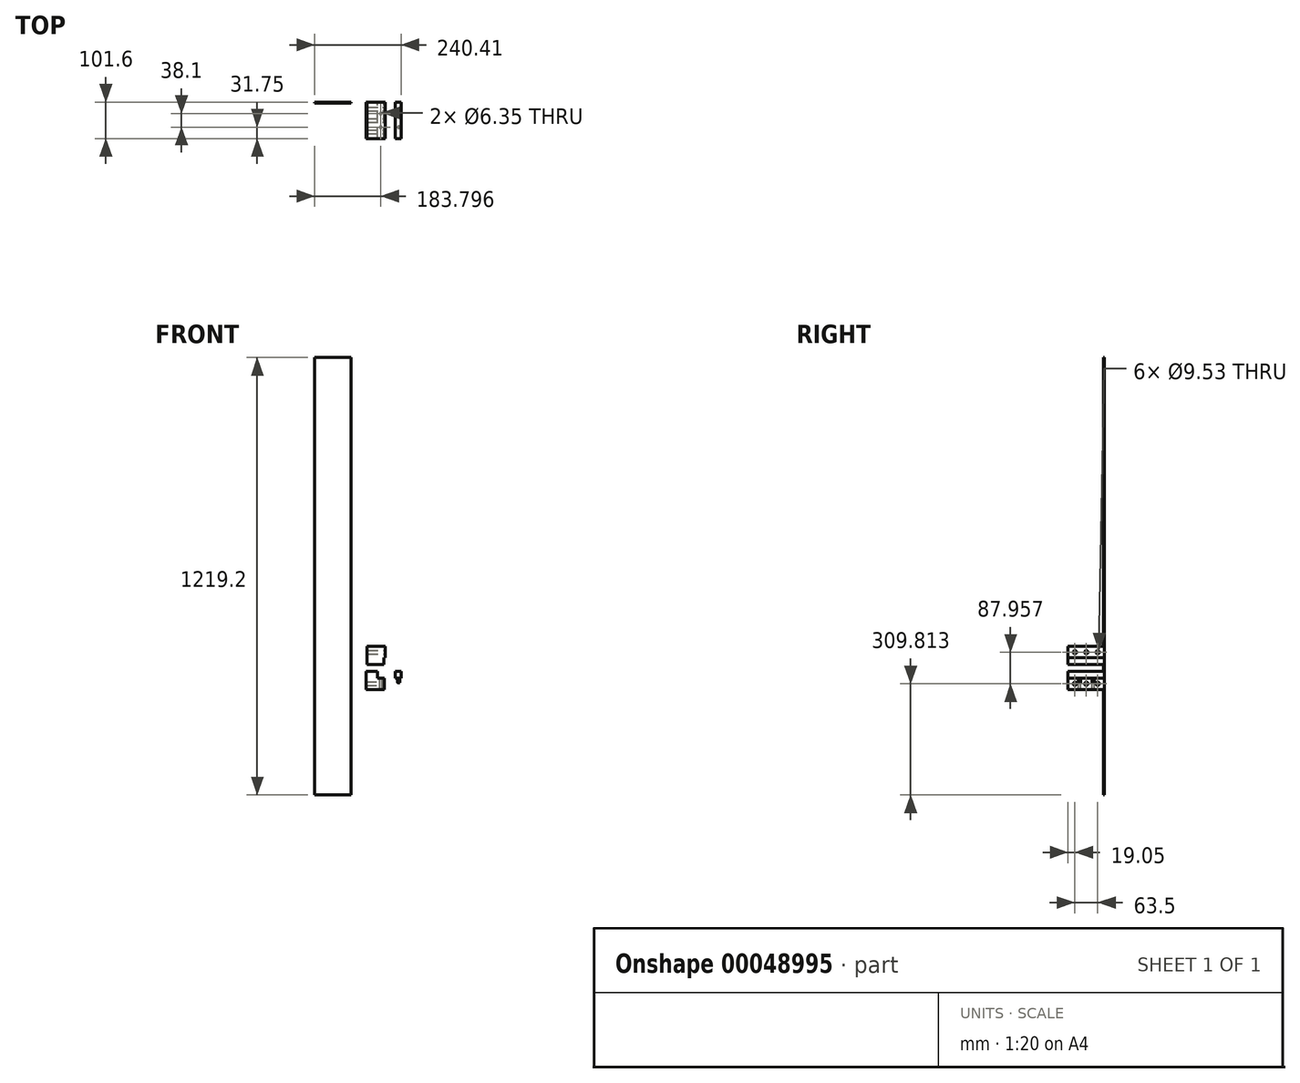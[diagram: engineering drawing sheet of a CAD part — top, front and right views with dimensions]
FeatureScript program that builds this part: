
annotation { "Feature Type Name" : "Feature", "Feature Type Description" : "" }
export const myFeature = defineFeature(function(context is Context, id is Id, definition is map)
    precondition{}
    {
        {
            var Q0;
            Q0=qCreatedBy(makeId("Front.planeOp"),FACE);
            var sketch = newSketch(context, id + "F0", { "sketchPlane" : qUnion([Q0])});
            skLineSegment(sketch, "E0", {"start": v(-72.63, 46.09) * mm, "end": v(-72.63, -4.71) * mm});
            skLineSegment(sketch, "E1", {"start": v(-72.63, -4.71) * mm, "end": v(-21.83, -4.71) * mm});
            skLineSegment(sketch, "E2", {"start": v(-21.83, -4.71) * mm, "end": v(-21.83, 27.04) * mm});
            skLineSegment(sketch, "E3", {"start": v(-21.83, 27.04) * mm, "end": v(-40.88, 27.04) * mm});
            skLineSegment(sketch, "E4", {"start": v(-40.88, 27.04) * mm, "end": v(-40.88, 46.09) * mm});
            skLineSegment(sketch, "E5", {"start": v(-40.88, 46.09) * mm, "end": v(-72.63, 46.09) * mm});
            skSolve(sketch);
        }
        {
            var Q0;
            Q0 = qSketchRegion(id + "F0", true);
            extrude(context, id + "F1", {"entities" : qUnion([Q0]), "depth" : 101.6 * mm});
        }
        {
            var Q0;
            Q0=makeQuery(id+"F1.opExtrude","SWEPT_FACE",FACE,{"disambiguationData":[OSD([sQuery(id+"F0.wireOp",EDGE,"E3")])]});
            var sketch = newSketch(context, id + "F2", { "sketchPlane" : qUnion([Q0])});
            skLineSegment(sketch, "E6.bottom", {"start": v(-21.83, -101.6) * mm, "end": v(-31.35, -101.6) * mm});
            skLineSegment(sketch, "E6.top", {"start": v(-21.83, -69.85) * mm, "end": v(-31.35, -69.85) * mm});
            skLineSegment(sketch, "E6.left", {"start": v(-21.83, -101.6) * mm, "end": v(-21.83, -69.85) * mm});
            skLineSegment(sketch, "E6.right", {"start": v(-31.35, -101.6) * mm, "end": v(-31.35, -69.85) * mm});
            skLineSegment(sketch, "E7.bottom", {"start": v(-21.83, 0) * mm, "end": v(-31.35, 0) * mm});
            skLineSegment(sketch, "E7.top", {"start": v(-21.83, -31.75) * mm, "end": v(-31.35, -31.75) * mm});
            skLineSegment(sketch, "E7.left", {"start": v(-21.83, 0) * mm, "end": v(-21.83, -31.75) * mm});
            skLineSegment(sketch, "E7.right", {"start": v(-31.35, 0) * mm, "end": v(-31.35, -31.75) * mm});
            skSolve(sketch);
        }
        {
            var Q0;
            Q0=sQuery(id+"F2.wireOp",VERTEX,"E6.top.end");
            var Q1;
            Q1=sQuery(id+"F2.wireOp",VERTEX,"E7.right.end");
            var Q2;
            Q2=makeQuery(id+"F1.opExtrude","SWEPT_BODY",BODY,{"disambiguationData":[OSD([sQuery(id+"F0.wireOp",EDGE,"E0"),sQuery(id+"F0.wireOp",EDGE,"E1"),sQuery(id+"F0.wireOp",EDGE,"E2"),sQuery(id+"F0.wireOp",EDGE,"E3"),sQuery(id+"F0.wireOp",EDGE,"E4"),sQuery(id+"F0.wireOp",EDGE,"E5")])]});
            hole(context, id + "F3", {"style" : HoleStyle.SIMPLE, "holeDiameter" : 6.35 * mm, "endStyle" : HoleEndStyle.THROUGH, "locations" : qUnion([Q0, Q1]), "scope" : qUnion([Q2])});
        }
        {
            var Q0;
            Q0=makeQuery(id+"F1.opExtrude","SWEPT_FACE",FACE,{"disambiguationData":[OSD([sQuery(id+"F0.wireOp",EDGE,"E2")])]});
            var sketch = newSketch(context, id + "F4", { "sketchPlane" : qUnion([Q0])});
            skLineSegment(sketch, "E8.bottom", {"start": v(-101.6, -4.71) * mm, "end": v(-82.55, -4.71) * mm});
            skLineSegment(sketch, "E8.top", {"start": v(-101.6, 11.16) * mm, "end": v(-82.55, 11.16) * mm});
            skLineSegment(sketch, "E8.left", {"start": v(-101.6, -4.71) * mm, "end": v(-101.6, 11.16) * mm});
            skLineSegment(sketch, "E8.right", {"start": v(-82.55, -4.71) * mm, "end": v(-82.55, 11.16) * mm});
            skLineSegment(sketch, "E9.bottom", {"start": v(0, -4.71) * mm, "end": v(-50.8, -4.71) * mm});
            skLineSegment(sketch, "E9.top", {"start": v(0, 11.16) * mm, "end": v(-50.8, 11.16) * mm});
            skLineSegment(sketch, "E9.left", {"start": v(0, -4.71) * mm, "end": v(0, 11.16) * mm});
            skLineSegment(sketch, "E9.right", {"start": v(-50.8, -4.71) * mm, "end": v(-50.8, 11.16) * mm});
            skLineSegment(sketch, "E10.bottom", {"start": v(0, -4.71) * mm, "end": v(-25.4, -4.71) * mm});
            skLineSegment(sketch, "E10.top", {"start": v(0, 11.16) * mm, "end": v(-25.4, 11.16) * mm});
            skLineSegment(sketch, "E10.right", {"start": v(-25.4, -4.71) * mm, "end": v(-25.4, 11.16) * mm});
            skLineSegment(sketch, "E11.bottom", {"start": v(0, -4.71) * mm, "end": v(-19.05, -4.71) * mm});
            skLineSegment(sketch, "E11.top", {"start": v(0, 11.16) * mm, "end": v(-19.05, 11.16) * mm});
            skLineSegment(sketch, "E11.right", {"start": v(-19.05, -4.71) * mm, "end": v(-19.05, 11.16) * mm});
            skSolve(sketch);
        }
        {
            var Q0;
            Q0=sQuery(id+"F4.wireOp",VERTEX,"E8.right.end");
            var Q1;
            Q1=sQuery(id+"F4.wireOp",VERTEX,"E9.right.end");
            var Q2;
            Q2=sQuery(id+"F4.wireOp",VERTEX,"E11.right.end");
            var Q3;
            Q3=makeQuery(id+"F1.opExtrude","SWEPT_BODY",BODY,{"disambiguationData":[OSD([sQuery(id+"F0.wireOp",EDGE,"E0"),sQuery(id+"F0.wireOp",EDGE,"E1"),sQuery(id+"F0.wireOp",EDGE,"E2"),sQuery(id+"F0.wireOp",EDGE,"E3"),sQuery(id+"F0.wireOp",EDGE,"E4"),sQuery(id+"F0.wireOp",EDGE,"E5")])]});
            hole(context, id + "F5", {"style" : HoleStyle.SIMPLE, "holeDiameter" : 9.52 * mm, "endStyle" : HoleEndStyle.THROUGH, "locations" : qUnion([Q0, Q1, Q2]), "scope" : qUnion([Q3])});
        }
        {
            var Q0;
            Q0=qCreatedBy(makeId("Front.planeOp"),FACE);
            var sketch = newSketch(context, id + "F6", { "sketchPlane" : qUnion([Q0])});
            skLineSegment(sketch, "E12.bottom", {"start": v(9.39, 45.44) * mm, "end": v(25.26, 45.44) * mm});
            skLineSegment(sketch, "E12.top", {"start": v(9.39, 26.39) * mm, "end": v(25.26, 26.39) * mm});
            skLineSegment(sketch, "E12.left", {"start": v(9.39, 45.44) * mm, "end": v(9.39, 26.39) * mm});
            skLineSegment(sketch, "E12.right", {"start": v(25.26, 45.44) * mm, "end": v(25.26, 26.39) * mm});
            skSolve(sketch);
        }
        {
            var Q0;
            Q0 = qSketchRegion(id + "F6", true);
            extrude(context, id + "F7", {"entities" : qUnion([Q0]), "depth" : 101.6 * mm});
        }
        {
            var Q0;
            Q0=makeQuery(id+"F7.opExtrude","SWEPT_FACE",FACE,{"disambiguationData":[OSD([sQuery(id+"F6.wireOp",EDGE,"E12.top")])]});
            var sketch = newSketch(context, id + "F8", { "sketchPlane" : qUnion([Q0])});
            skLineSegment(sketch, "E13.bottom", {"start": v(25.26, 101.6) * mm, "end": v(15.74, 101.6) * mm});
            skLineSegment(sketch, "E13.left", {"start": v(25.26, 101.6) * mm, "end": v(25.26, 69.85) * mm});
            skLineSegment(sketch, "E14.bottom", {"start": v(25.26, 0) * mm, "end": v(15.74, 0) * mm});
            skLineSegment(sketch, "E14.left", {"start": v(25.26, 0) * mm, "end": v(25.26, 31.75) * mm});
            skCircle(sketch, "E15", {"center": v(18.91, 69.85) * mm, "radius": 3.18 * mm});
            skCircle(sketch, "E16", {"center": v(18.91, 31.75) * mm, "radius": 3.18 * mm});
            skSolve(sketch);
        }
        {
            var Q0;
            Q0=makeQuery(id+"F8.imprint","IMPRINT",FACE,{"disambiguationData":[TD([[makeQuery(id+"F8.imprint","IMPRINT",EDGE,{"derivedFrom":sQuery(id+"F8.wireOp",EDGE,"E15")}),1.0]])]});
            var Q1;
            Q1=makeQuery(id+"F8.imprint","IMPRINT",FACE,{"disambiguationData":[TD([[makeQuery(id+"F8.imprint","IMPRINT",EDGE,{"derivedFrom":sQuery(id+"F8.wireOp",EDGE,"E16")}),1.0]])]});
            extrude(context, id + "F9", {"entities" : qUnion([Q0, Q1]), "operationType" : NewBodyOperationType.ADD, "depth" : 12.7 * mm});
        }
        {
            var Q0;
            Q0=qCreatedBy(makeId("Front.planeOp"),FACE);
            var sketch = newSketch(context, id + "F10", { "sketchPlane" : qUnion([Q0])});
            skLineSegment(sketch, "E17.bottom", {"start": v(-69.64, 115) * mm, "end": v(-18.84, 115) * mm});
            skLineSegment(sketch, "E17.top", {"start": v(-69.64, 64.2) * mm, "end": v(-22.02, 64.2) * mm});
            skLineSegment(sketch, "E17.left", {"start": v(-69.64, 115) * mm, "end": v(-69.64, 64.2) * mm});
            skLineSegment(sketch, "E17.right", {"start": v(-18.84, 115) * mm, "end": v(-18.84, 83.24) * mm});
            skLineSegment(sketch, "E18.bottom", {"start": v(-18.84, 83.24) * mm, "end": v(-22.02, 83.24) * mm});
            skLineSegment(sketch, "E18.right", {"start": v(-22.02, 83.24) * mm, "end": v(-22.02, 64.2) * mm});
            skSolve(sketch);
        }
        {
            var Q0;
            Q0 = qSketchRegion(id + "F10", true);
            extrude(context, id + "F11", {"entities" : qUnion([Q0]), "depth" : 101.6 * mm});
        }
        {
            var Q0;
            Q0=makeQuery(id+"F11.opExtrude","SWEPT_FACE",FACE,{"disambiguationData":[OSD([sQuery(id+"F10.wireOp",EDGE,"E17.right")])]});
            var sketch = newSketch(context, id + "F12", { "sketchPlane" : qUnion([Q0])});
            skLineSegment(sketch, "E19.bottom", {"start": v(-101.6, 115) * mm, "end": v(-82.55, 115) * mm});
            skLineSegment(sketch, "E19.top", {"start": v(-101.6, 99.12) * mm, "end": v(-82.55, 99.12) * mm});
            skLineSegment(sketch, "E19.left", {"start": v(-101.6, 115) * mm, "end": v(-101.6, 99.12) * mm});
            skLineSegment(sketch, "E19.right", {"start": v(-82.55, 115) * mm, "end": v(-82.55, 99.12) * mm});
            skLineSegment(sketch, "E20.bottom", {"start": v(0, 115) * mm, "end": v(-50.8, 115) * mm});
            skLineSegment(sketch, "E20.top", {"start": v(0, 99.12) * mm, "end": v(-50.8, 99.12) * mm});
            skLineSegment(sketch, "E20.left", {"start": v(0, 115) * mm, "end": v(0, 99.12) * mm});
            skLineSegment(sketch, "E20.right", {"start": v(-50.8, 115) * mm, "end": v(-50.8, 99.12) * mm});
            skLineSegment(sketch, "E21.bottom", {"start": v(0, 115) * mm, "end": v(-19.05, 115) * mm});
            skLineSegment(sketch, "E21.top", {"start": v(0, 99.12) * mm, "end": v(-19.05, 99.12) * mm});
            skLineSegment(sketch, "E21.right", {"start": v(-19.05, 115) * mm, "end": v(-19.05, 99.12) * mm});
            skSolve(sketch);
        }
        {
            var Q0;
            Q0=sQuery(id+"F12.wireOp",VERTEX,"E19.right.end");
            var Q1;
            Q1=sQuery(id+"F12.wireOp",VERTEX,"E20.top.end");
            var Q2;
            Q2=sQuery(id+"F12.wireOp",VERTEX,"E21.right.end");
            var Q3;
            Q3=makeQuery(id+"F11.opExtrude","SWEPT_BODY",BODY,{"disambiguationData":[OSD([sQuery(id+"F10.wireOp",EDGE,"E17.bottom"),sQuery(id+"F10.wireOp",EDGE,"E17.top"),sQuery(id+"F10.wireOp",EDGE,"E17.left"),sQuery(id+"F10.wireOp",EDGE,"E17.right"),sQuery(id+"F10.wireOp",EDGE,"E18.bottom"),sQuery(id+"F10.wireOp",EDGE,"E18.right")])]});
            hole(context, id + "F13", {"style" : HoleStyle.SIMPLE, "holeDiameter" : 9.52 * mm, "endStyle" : HoleEndStyle.THROUGH, "locations" : qUnion([Q0, Q1, Q2]), "scope" : qUnion([Q3])});
        }
        {
            var Q0;
            Q0=qCreatedBy(makeId("Front.planeOp"),FACE);
            var sketch = newSketch(context, id + "F14", { "sketchPlane" : qUnion([Q0])});
            skLineSegment(sketch, "E22.bottom", {"start": v(-215.15, 920.55) * mm, "end": v(-113.55, 920.55) * mm});
            skLineSegment(sketch, "E22.top", {"start": v(-215.15, -298.65) * mm, "end": v(-113.55, -298.65) * mm});
            skLineSegment(sketch, "E22.left", {"start": v(-215.15, 920.55) * mm, "end": v(-215.15, -298.65) * mm});
            skLineSegment(sketch, "E22.right", {"start": v(-113.55, 920.55) * mm, "end": v(-113.55, -298.65) * mm});
            skSolve(sketch);
        }
        {
            var Q0;
            Q0=makeQuery(id+"F14.imprint","IMPRINT",FACE,{"disambiguationData":[TD([[makeQuery(id+"F14.imprint","IMPRINT",EDGE,{"derivedFrom":sQuery(id+"F14.wireOp",EDGE,"E22.bottom")}),-1.0]])]});
            extrude(context, id + "F15", {"entities" : qUnion([Q0]), "depth" : 3.17 * mm});
        }
    });
